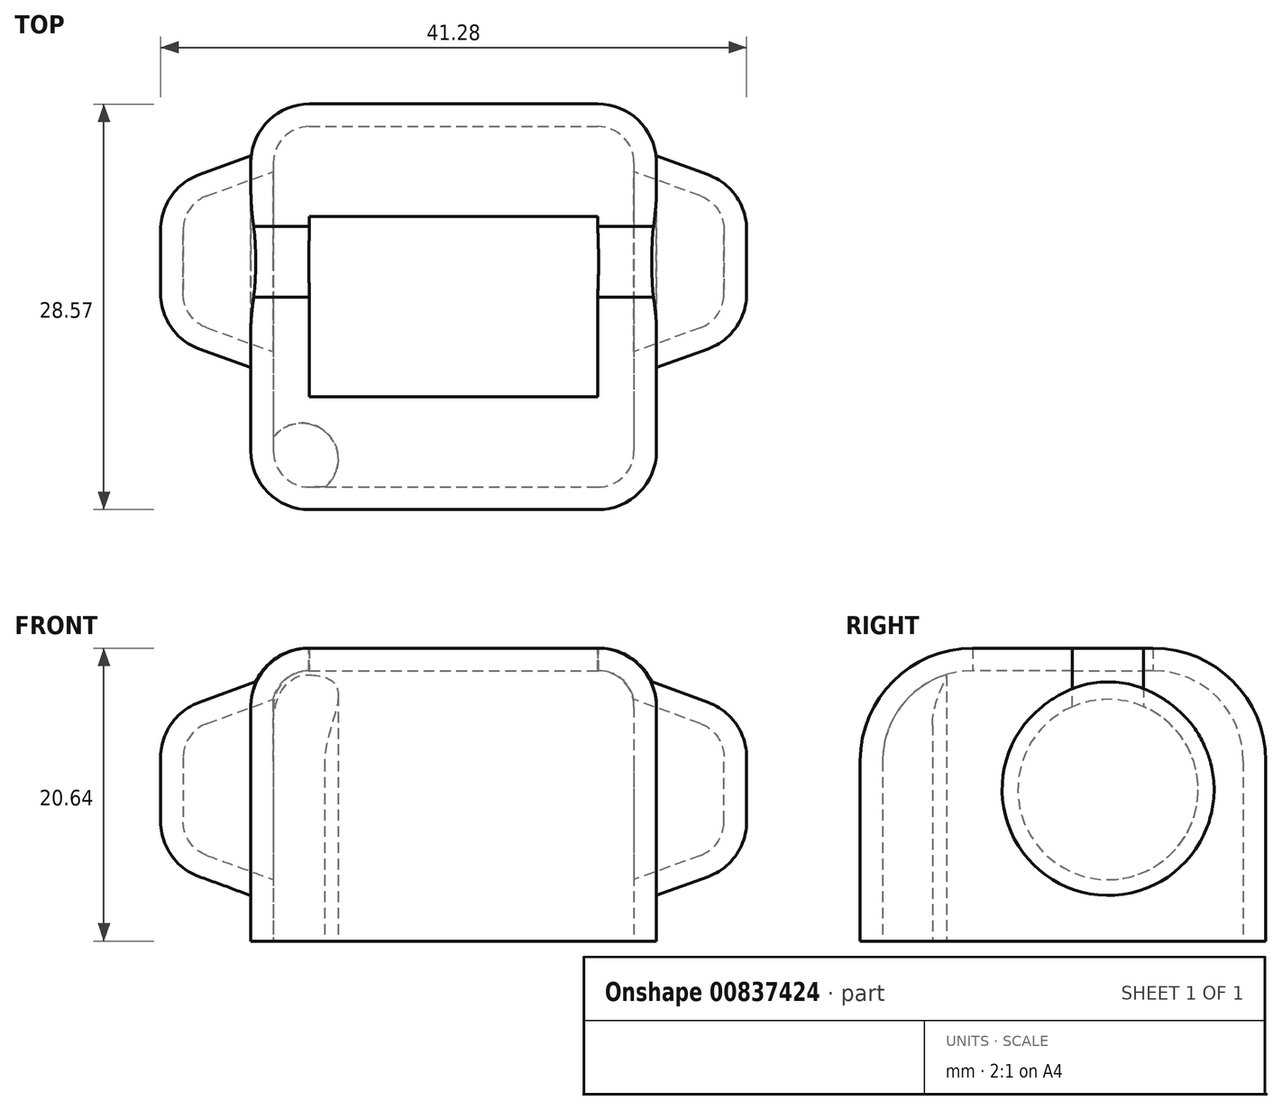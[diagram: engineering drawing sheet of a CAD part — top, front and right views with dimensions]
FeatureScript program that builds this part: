
annotation { "Feature Type Name" : "Feature", "Feature Type Description" : "" }
export const myFeature = defineFeature(function(context is Context, id is Id, definition is map)
    precondition{}
    {
        {
            var Q0;
            Q0=qCreatedBy(makeId("Top.planeOp"),FACE);
            var sketch = newSketch(context, id + "F0", { "sketchPlane" : qUnion([Q0])});
            skLineSegment(sketch, "E0.bottom", {"start": v(-7.71, 5.68) * mm, "end": v(17.69, 5.68) * mm});
            skLineSegment(sketch, "E0.top", {"start": v(-7.71, -19.72) * mm, "end": v(17.69, -19.72) * mm});
            skLineSegment(sketch, "E0.left", {"start": v(-7.71, 5.68) * mm, "end": v(-7.71, -19.72) * mm});
            skLineSegment(sketch, "E0.right", {"start": v(17.69, 5.68) * mm, "end": v(17.69, -19.72) * mm});
            skSolve(sketch);
        }
        {
            var Q0;
            Q0=makeQuery(id+"F0.imprint","IMPRINT",FACE,{"disambiguationData":[TD([[makeQuery(id+"F0.imprint","IMPRINT",EDGE,{"derivedFrom":sQuery(id+"F0.wireOp",EDGE,"E0.bottom")}),-1.0]])]});
            extrude(context, id + "F1", {"entities" : qUnion([Q0]), "depth" : 19.05 * mm, "offsetDistance" : 25.4 * mm});
        }
        {
            var Q0;
            Q0=makeQuery(id+"F1.opExtrude","CAP_EDGE",EDGE,{"disambiguationData":[OSD([sQuery(id+"F0.wireOp",EDGE,"E0.top")])],"isStart":false});
            var Q1;
            Q1=makeQuery(id+"F1.opExtrude","CAP_EDGE",EDGE,{"disambiguationData":[OSD([sQuery(id+"F0.wireOp",EDGE,"E0.bottom")])],"isStart":false});
            fillet(context, id + "F2", {"entities" : qUnion([Q0, Q1]), "radius" : 6.35 * mm, "tangentPropagation" : true, "allowEdgeOverflow" : false});
        }
        {
            var Q0;
            Q0=makeQuery(id+"F1.opExtrude","SWEPT_FACE",FACE,{"disambiguationData":[OSD([sQuery(id+"F0.wireOp",EDGE,"E0.right")])]});
            var sketch = newSketch(context, id + "F3", { "sketchPlane" : qUnion([Q0])});
            skSolve(sketch);
        }
        {
            var Q0;
            {var subQ0=sQuery(id+"F0.wireOp",EDGE,"E0.right");Q0=makeQuery(id+"F3.imprint","IMPRINT",FACE,{"disambiguationData":[TD([[makeQuery(id+"F3.imprint","IMPRINT",EDGE,{"derivedFrom":makeQuery(id+"F1.opExtrude","CAP_EDGE",EDGE,{"disambiguationData":[OSD([subQ0])],"isStart":true})}),-1.0]])]});}
            var sketch = newSketch(context, id + "F4", { "sketchPlane" : qUnion([Q0])});
            skCircle(sketch, "E1", {"center": v(-3.85, 10.68) * mm, "radius": 6.35 * mm});
            skSolve(sketch);
        }
        {
            var Q0;
            Q0 = qSketchRegion(id + "F4", true);
            extrude(context, id + "F5", {"entities" : qUnion([Q0]), "operationType" : NewBodyOperationType.ADD, "depth" : 6.35 * mm, "offsetDistance" : 25.4 * mm, "hasDraft" : true, "draftAngle" : 20 * degree, "draftPullDirection" : true});
        }
        {
            var Q0;
            {var subQ0=sQuery(id+"F0.wireOp",EDGE,"E0.right");Q0=makeQuery(id+"F3.imprint","IMPRINT",FACE,{"disambiguationData":[TD([[makeQuery(id+"F3.imprint","IMPRINT",EDGE,{"derivedFrom":makeQuery(id+"F1.opExtrude","CAP_EDGE",EDGE,{"disambiguationData":[OSD([subQ0])],"isStart":true})}),-1.0]])]});}
            cPlane(context, id + "F6", {"entities" : qUnion([Q0]), "cplaneType" : CPlaneType.OFFSET, "offset" : 12.7 * mm, "oppositeDirection" : true, "width" : 152.4 * mm, "height" : 152.4 * mm});
        }
        {
            var Q0;
            Q0=makeQuery(id+"F1.opExtrude","SWEPT_BODY",BODY,{"disambiguationData":[OSD([sQuery(id+"F0.wireOp",EDGE,"E0.bottom"),sQuery(id+"F0.wireOp",EDGE,"E0.top"),sQuery(id+"F0.wireOp",EDGE,"E0.left"),sQuery(id+"F0.wireOp",EDGE,"E0.right")])]});
            var Q1;
            Q1=qCreatedBy(id+"F6.planeOp",FACE);
            mirror(context, id + "F7", {"operationType" : NewBodyOperationType.ADD, "entities" : qUnion([Q0]), "mirrorPlane" : qUnion([Q1])});
        }
        {
            var Q0;
            Q0=makeQuery(id+"F5.opExtrude","CAP_EDGE",EDGE,{"disambiguationData":[OSD([sQuery(id+"F4.wireOp",EDGE,"E1")])],"isStart":false});
            var Q1;
            Q1=makeQuery(id+"F7.opPattern","COPY",EDGE,{"derivedFrom":makeQuery(id+"F5.opExtrude","CAP_EDGE",EDGE,{"disambiguationData":[OSD([sQuery(id+"F4.wireOp",EDGE,"E1")])],"isStart":false}),"instanceName":"1"});
            fillet(context, id + "F8", {"entities" : qUnion([Q0, Q1]), "radius" : 2.54 * mm, "tangentPropagation" : true, "allowEdgeOverflow" : false});
        }
        {
            var Q0;
            Q0=makeQuery(id+"F1.opExtrude","SWEPT_EDGE",EDGE,{"disambiguationData":[OSD([sQuery(id+"F0.wireOp",EDGE,"E0.top"),sQuery(id+"F0.wireOp",EDGE,"E0.right")])]});
            var Q1;
            Q1=makeQuery(id+"F1.opExtrude","SWEPT_EDGE",EDGE,{"disambiguationData":[OSD([sQuery(id+"F0.wireOp",EDGE,"E0.top"),sQuery(id+"F0.wireOp",EDGE,"E0.left")])]});
            fillet(context, id + "F9", {"entities" : qUnion([Q0, Q1]), "radius" : 2.54 * mm, "tangentPropagation" : true, "allowEdgeOverflow" : false});
        }
        {
            var Q0;
            Q0=makeQuery(id+"F1.opExtrude","CAP_FACE",FACE,{"disambiguationData":[OSD([sQuery(id+"F0.wireOp",EDGE,"E0.bottom"),sQuery(id+"F0.wireOp",EDGE,"E0.top"),sQuery(id+"F0.wireOp",EDGE,"E0.left"),sQuery(id+"F0.wireOp",EDGE,"E0.right")])],"isStart":true});
            shell(context, id + "F10", {"entities" : qUnion([Q0]), "thickness" : 1.59 * mm, "oppositeDirection" : true});
        }
        {
            var Q0;
            Q0=makeQuery(id+"F10.opShell","OFFSET_FACE",FACE,{"disambiguationData":[OSD([sQuery(id+"F0.wireOp",EDGE,"E0.bottom"),sQuery(id+"F0.wireOp",EDGE,"E0.top"),sQuery(id+"F0.wireOp",EDGE,"E0.left"),sQuery(id+"F0.wireOp",EDGE,"E0.right")])]});
            extrude(context, id + "F11", {"entities" : qUnion([Q0]), "endBound" : BoundingType.UP_TO_NEXT, "oppositeDirection" : true, "depth" : 25.4 * mm, "offsetDistance" : 25.4 * mm});
        }
        {
            var Q0;
            Q0=makeQuery(id+"F1.opExtrude","CAP_FACE",FACE,{"disambiguationData":[OSD([sQuery(id+"F0.wireOp",EDGE,"E0.bottom"),sQuery(id+"F0.wireOp",EDGE,"E0.top"),sQuery(id+"F0.wireOp",EDGE,"E0.left"),sQuery(id+"F0.wireOp",EDGE,"E0.right")])],"isStart":true});
            var sketch = newSketch(context, id + "F12", { "sketchPlane" : qUnion([Q0])});
            skCircle(sketch, "E2", {"center": v(-5.69, 17.75) * mm, "radius": 2.54 * mm});
            skSolve(sketch);
        }
        {
            var Q0;
            {var subQ0=sQuery(id+"F12.wireOp",EDGE,"E2");var subQ1=sQuery(id+"F0.wireOp",EDGE,"E0.top");var subQ2=makeQuery(id+"F12.imprint","INTERSECT",VERTEX,{"derivedFrom":[makeQuery(id+"F10.opShell","OFFSET_EDGE",EDGE,{"disambiguationData":[OSD([subQ1]),TDD([makeQuery(id+"F1.opExtrude","CAP_EDGE",EDGE,{"disambiguationData":[OSD([subQ1])],"isStart":true})])]}),subQ0]});Q0=makeQuery(id+"F12.imprint","IMPRINT",FACE,{"disambiguationData":[TD([[makeQuery(id+"F12.imprint","IMPRINT",EDGE,{"disambiguationData":[TD([[subQ2,1.0]])],"derivedFrom":subQ0}),1.0]])]});}
            extrude(context, id + "F13", {"entities" : qUnion([Q0]), "endBound" : BoundingType.UP_TO_NEXT, "oppositeDirection" : true, "depth" : 25.4 * mm, "offsetDistance" : 25.4 * mm});
        }
    });
